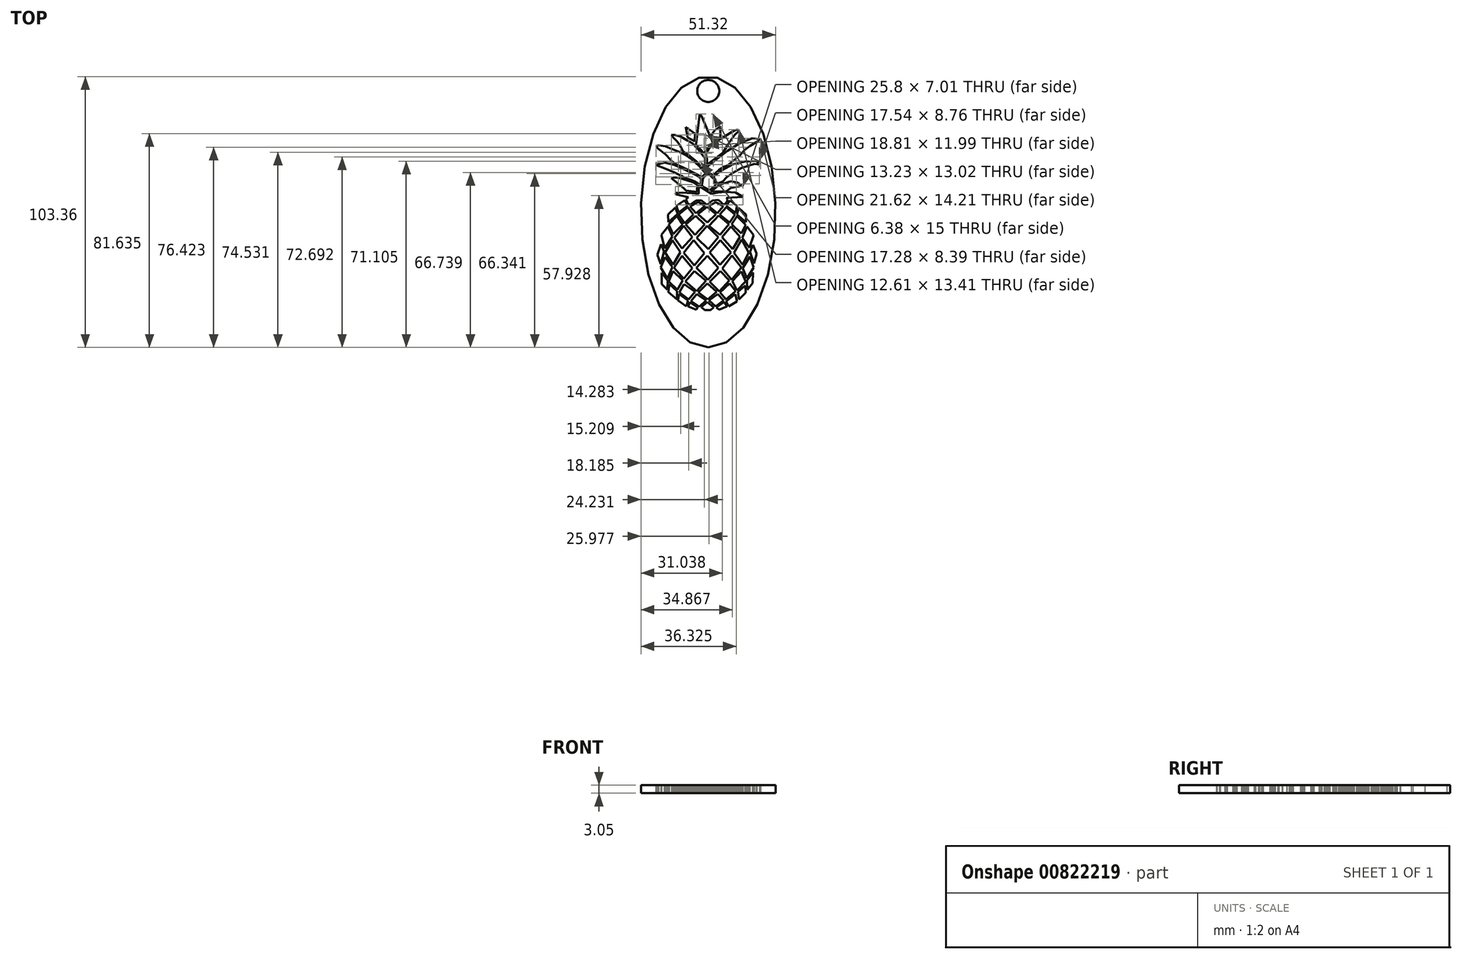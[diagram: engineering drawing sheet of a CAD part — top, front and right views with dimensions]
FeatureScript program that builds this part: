
annotation { "Feature Type Name" : "Feature", "Feature Type Description" : "" }
export const myFeature = defineFeature(function(context is Context, id is Id, definition is map)
    precondition{}
    {
        {
            var Q0;
            Q0=qCreatedBy(makeId("Top.planeOp"),FACE);
            var sketch = newSketch(context, id + "F0", { "sketchPlane" : qUnion([Q0])});
            skLineSegment(sketch, "E0", {"start": v(-25.66, -1.5) * mm, "end": v(-25.25, -6.5) * mm});
            skLineSegment(sketch, "E1", {"start": v(-25.25, -6.5) * mm, "end": v(-19.48, -1.16) * mm});
            skLineSegment(sketch, "E2", {"start": v(-19.48, -1.16) * mm, "end": v(-21, 2.9) * mm});
            skLineSegment(sketch, "E3", {"start": v(-21, 2.9) * mm, "end": v(-25.66, -1.5) * mm});
            skLineSegment(sketch, "E4", {"start": v(-20.22, 3.8) * mm, "end": v(-18.77, -0.42) * mm});
            skLineSegment(sketch, "E5", {"start": v(-18.77, -0.42) * mm, "end": v(-13.06, 4.15) * mm});
            skLineSegment(sketch, "E6", {"start": v(-13.06, 4.15) * mm, "end": v(-15.05, 7.52) * mm});
            skLineSegment(sketch, "E7", {"start": v(-15.05, 7.52) * mm, "end": v(-20.22, 3.8) * mm});
            skLineSegment(sketch, "E8", {"start": v(-18.89, -1.52) * mm, "end": v(-14.98, -7.06) * mm});
            skLineSegment(sketch, "E9", {"start": v(-14.98, -7.06) * mm, "end": v(-9.4, -1.52) * mm});
            skLineSegment(sketch, "E10", {"start": v(-9.4, -1.52) * mm, "end": v(-13.06, 3.14) * mm});
            skLineSegment(sketch, "E11", {"start": v(-13.06, 3.14) * mm, "end": v(-18.89, -1.52) * mm});
            skLineSegment(sketch, "E12", {"start": v(-25.2, -7.88) * mm, "end": v(-22.35, -14.06) * mm});
            skLineSegment(sketch, "E13", {"start": v(-22.35, -14.06) * mm, "end": v(-16.27, -7.88) * mm});
            skLineSegment(sketch, "E14", {"start": v(-16.27, -7.88) * mm, "end": v(-19.8, -2.51) * mm});
            skLineSegment(sketch, "E15", {"start": v(-19.8, -2.51) * mm, "end": v(-25.2, -7.88) * mm});
            skLineSegment(sketch, "E16", {"start": v(-25.66, -9.17) * mm, "end": v(-29.74, -14.43) * mm});
            skLineSegment(sketch, "E17", {"start": v(-29.74, -14.43) * mm, "end": v(-27.7, -23.26) * mm});
            skLineSegment(sketch, "E18", {"start": v(-27.7, -23.26) * mm, "end": v(-22.9, -15.5) * mm});
            skLineSegment(sketch, "E19", {"start": v(-22.9, -15.5) * mm, "end": v(-25.66, -9.17) * mm});
            skLineSegment(sketch, "E20", {"start": v(-21.48, -16.47) * mm, "end": v(-16.64, -23.26) * mm});
            skLineSegment(sketch, "E21", {"start": v(-16.64, -23.26) * mm, "end": v(-10.19, -16.03) * mm});
            skLineSegment(sketch, "E22", {"start": v(-10.19, -16.03) * mm, "end": v(-15.65, -8.87) * mm});
            skLineSegment(sketch, "E23", {"start": v(-15.65, -8.87) * mm, "end": v(-21.48, -16.47) * mm});
            skLineSegment(sketch, "E24", {"start": v(-30, -20.49) * mm, "end": v(-32.38, -27.19) * mm});
            skLineSegment(sketch, "E25", {"start": v(-32.38, -27.19) * mm, "end": v(-30.27, -33.09) * mm});
            skLineSegment(sketch, "E26", {"start": v(-30.27, -33.09) * mm, "end": v(-28.16, -24.99) * mm});
            skLineSegment(sketch, "E27", {"start": v(-28.16, -24.99) * mm, "end": v(-30, -20.49) * mm});
            skLineSegment(sketch, "E28", {"start": v(-27.43, -25.7) * mm, "end": v(-22.9, -17.8) * mm});
            skLineSegment(sketch, "E29", {"start": v(-22.9, -17.8) * mm, "end": v(-17.62, -25.44) * mm});
            skLineSegment(sketch, "E30", {"start": v(-17.62, -25.44) * mm, "end": v(-22.3, -33.55) * mm});
            skLineSegment(sketch, "E31", {"start": v(-22.3, -33.55) * mm, "end": v(-27.43, -25.7) * mm});
            skLineSegment(sketch, "E32", {"start": v(-29.58, -38.67) * mm, "end": v(-25.77, -43.74) * mm});
            skLineSegment(sketch, "E33", {"start": v(-25.77, -43.74) * mm, "end": v(-25.9, -49.5) * mm});
            skLineSegment(sketch, "E34", {"start": v(-25.9, -49.5) * mm, "end": v(-29.58, -45.83) * mm});
            skLineSegment(sketch, "E35", {"start": v(-29.58, -45.83) * mm, "end": v(-29.58, -38.67) * mm});
            skLineSegment(sketch, "E36", {"start": v(-25.89, -42.39) * mm, "end": v(-22.9, -35.09) * mm});
            skLineSegment(sketch, "E37", {"start": v(-22.9, -35.09) * mm, "end": v(-27.43, -28.61) * mm});
            skLineSegment(sketch, "E38", {"start": v(-27.43, -28.61) * mm, "end": v(-30.13, -35.18) * mm});
            skLineSegment(sketch, "E39", {"start": v(-30.13, -35.18) * mm, "end": v(-25.89, -42.39) * mm});
            skLineSegment(sketch, "E40", {"start": v(-25.06, -44.25) * mm, "end": v(-22.28, -37.5) * mm});
            skLineSegment(sketch, "E41", {"start": v(-22.28, -37.5) * mm, "end": v(-16.15, -43.49) * mm});
            skLineSegment(sketch, "E42", {"start": v(-16.15, -43.49) * mm, "end": v(-19.57, -49.5) * mm});
            skLineSegment(sketch, "E43", {"start": v(-19.57, -49.5) * mm, "end": v(-25.06, -44.25) * mm});
            skLineSegment(sketch, "E44", {"start": v(-24.8, -45.83) * mm, "end": v(-19.76, -50.26) * mm});
            skLineSegment(sketch, "E45", {"start": v(-19.76, -50.26) * mm, "end": v(-19.76, -55.47) * mm});
            skLineSegment(sketch, "E46", {"start": v(-19.76, -55.47) * mm, "end": v(-25.36, -50.95) * mm});
            skLineSegment(sketch, "E47", {"start": v(-25.36, -50.95) * mm, "end": v(-24.8, -45.83) * mm});
            skLineSegment(sketch, "E48", {"start": v(-19.16, -56.23) * mm, "end": v(-18.61, -52.19) * mm});
            skLineSegment(sketch, "E49", {"start": v(-18.61, -52.19) * mm, "end": v(-12.83, -56.23) * mm});
            skLineSegment(sketch, "E50", {"start": v(-12.83, -56.23) * mm, "end": v(-13.84, -60) * mm});
            skLineSegment(sketch, "E51", {"start": v(-13.84, -60) * mm, "end": v(-19.16, -56.23) * mm});
            skLineSegment(sketch, "E52", {"start": v(-11.6, -57.29) * mm, "end": v(-6.67, -60.45) * mm});
            skLineSegment(sketch, "E53", {"start": v(-6.67, -60.45) * mm, "end": v(-7.6, -62.06) * mm});
            skLineSegment(sketch, "E54", {"start": v(-7.6, -62.06) * mm, "end": v(-12.92, -60) * mm});
            skLineSegment(sketch, "E55", {"start": v(-12.92, -60) * mm, "end": v(-11.6, -57.29) * mm});
            skLineSegment(sketch, "E56", {"start": v(-2.29, -62.43) * mm, "end": v(1.52, -62.43) * mm});
            skLineSegment(sketch, "E57", {"start": v(1.52, -62.43) * mm, "end": v(3.43, -60.6) * mm});
            skLineSegment(sketch, "E58", {"start": v(3.43, -60.6) * mm, "end": v(-0.54, -57.17) * mm});
            skLineSegment(sketch, "E59", {"start": v(-0.54, -57.17) * mm, "end": v(-4.5, -60.45) * mm});
            skLineSegment(sketch, "E60", {"start": v(-4.5, -60.45) * mm, "end": v(-2.29, -62.43) * mm});
            skLineSegment(sketch, "E61", {"start": v(-5.7, -60.25) * mm, "end": v(-1.49, -56.3) * mm});
            skLineSegment(sketch, "E62", {"start": v(-1.49, -56.3) * mm, "end": v(-7.34, -52.19) * mm});
            skLineSegment(sketch, "E63", {"start": v(-7.34, -52.19) * mm, "end": v(-11.06, -56.55) * mm});
            skLineSegment(sketch, "E64", {"start": v(-11.06, -56.55) * mm, "end": v(-5.7, -60.25) * mm});
            skLineSegment(sketch, "E65", {"start": v(6.85, -62.06) * mm, "end": v(11.9, -60) * mm});
            skLineSegment(sketch, "E66", {"start": v(11.9, -60) * mm, "end": v(10.08, -57.17) * mm});
            skLineSegment(sketch, "E67", {"start": v(10.08, -57.17) * mm, "end": v(5.15, -60.68) * mm});
            skLineSegment(sketch, "E68", {"start": v(5.15, -60.68) * mm, "end": v(6.85, -62.06) * mm});
            skLineSegment(sketch, "E69", {"start": v(4.67, -60) * mm, "end": v(9.8, -56.22) * mm});
            skLineSegment(sketch, "E70", {"start": v(9.8, -56.22) * mm, "end": v(5.95, -52.19) * mm});
            skLineSegment(sketch, "E71", {"start": v(0.4, -56.22) * mm, "end": v(4.67, -60) * mm});
            skLineSegment(sketch, "E72", {"start": v(12.93, -60.09) * mm, "end": v(18.23, -56.83) * mm});
            skLineSegment(sketch, "E73", {"start": v(18.23, -56.83) * mm, "end": v(17.22, -52.19) * mm});
            skLineSegment(sketch, "E74", {"start": v(17.22, -52.19) * mm, "end": v(11.26, -56.78) * mm});
            skLineSegment(sketch, "E75", {"start": v(11.26, -56.78) * mm, "end": v(12.93, -60.09) * mm});
            skLineSegment(sketch, "E76", {"start": v(19.52, -55.6) * mm, "end": v(23.67, -51.43) * mm});
            skLineSegment(sketch, "E77", {"start": v(23.67, -51.43) * mm, "end": v(23.5, -46.61) * mm});
            skLineSegment(sketch, "E78", {"start": v(23.5, -46.61) * mm, "end": v(18.83, -50.6) * mm});
            skLineSegment(sketch, "E79", {"start": v(18.83, -50.6) * mm, "end": v(19.52, -55.6) * mm});
            skLineSegment(sketch, "E80", {"start": v(24.87, -49.48) * mm, "end": v(28.22, -45.16) * mm});
            skLineSegment(sketch, "E81", {"start": v(28.22, -45.16) * mm, "end": v(28.52, -38.53) * mm});
            skLineSegment(sketch, "E82", {"start": v(28.52, -38.53) * mm, "end": v(24.7, -43.42) * mm});
            skLineSegment(sketch, "E83", {"start": v(24.7, -43.42) * mm, "end": v(24.87, -49.48) * mm});
            skLineSegment(sketch, "E84", {"start": v(24.7, -42.23) * mm, "end": v(28.81, -35.16) * mm});
            skLineSegment(sketch, "E85", {"start": v(28.81, -35.16) * mm, "end": v(26.61, -28.25) * mm});
            skLineSegment(sketch, "E86", {"start": v(26.61, -28.25) * mm, "end": v(21.88, -35.61) * mm});
            skLineSegment(sketch, "E87", {"start": v(21.88, -35.61) * mm, "end": v(24.7, -42.23) * mm});
            skLineSegment(sketch, "E88", {"start": v(29.1, -32.7) * mm, "end": v(30.74, -26.55) * mm});
            skLineSegment(sketch, "E89", {"start": v(30.74, -26.55) * mm, "end": v(28.5, -20.78) * mm});
            skLineSegment(sketch, "E90", {"start": v(28.5, -20.78) * mm, "end": v(26.59, -25.37) * mm});
            skLineSegment(sketch, "E91", {"start": v(26.59, -25.37) * mm, "end": v(29.1, -32.7) * mm});
            skLineSegment(sketch, "E92", {"start": v(26.08, -22.69) * mm, "end": v(28.81, -14.65) * mm});
            skLineSegment(sketch, "E93", {"start": v(28.81, -14.65) * mm, "end": v(24.54, -9.28) * mm});
            skLineSegment(sketch, "E94", {"start": v(24.54, -9.28) * mm, "end": v(21.68, -16.37) * mm});
            skLineSegment(sketch, "E95", {"start": v(21.68, -16.37) * mm, "end": v(26.08, -22.69) * mm});
            skLineSegment(sketch, "E96", {"start": v(20.99, -13.69) * mm, "end": v(23.83, -8.2) * mm});
            skLineSegment(sketch, "E97", {"start": v(23.83, -8.2) * mm, "end": v(18.2, -2.6) * mm});
            skLineSegment(sketch, "E98", {"start": v(18.2, -2.6) * mm, "end": v(14.88, -7.74) * mm});
            skLineSegment(sketch, "E99", {"start": v(14.88, -7.74) * mm, "end": v(20.99, -13.69) * mm});
            skLineSegment(sketch, "E100", {"start": v(24.02, -6.48) * mm, "end": v(24.02, -1.54) * mm});
            skLineSegment(sketch, "E101", {"start": v(24.02, -1.54) * mm, "end": v(19.36, 2.68) * mm});
            skLineSegment(sketch, "E102", {"start": v(19.36, 2.68) * mm, "end": v(18.28, -1.59) * mm});
            skLineSegment(sketch, "E103", {"start": v(18.28, -1.59) * mm, "end": v(24.02, -6.48) * mm});
            skLineSegment(sketch, "E104", {"start": v(11.46, 3.92) * mm, "end": v(13.8, 7.2) * mm});
            skLineSegment(sketch, "E105", {"start": v(13.8, 7.2) * mm, "end": v(18.28, 3.92) * mm});
            skLineSegment(sketch, "E106", {"start": v(18.28, 3.92) * mm, "end": v(17.48, -0.47) * mm});
            skLineSegment(sketch, "E107", {"start": v(17.48, -0.47) * mm, "end": v(11.46, 3.92) * mm});
            skLineSegment(sketch, "E108", {"start": v(5.77, -0.72) * mm, "end": v(9.53, 3.67) * mm});
            skLineSegment(sketch, "E109", {"start": v(9.53, 3.67) * mm, "end": v(4.63, 6.14) * mm});
            skLineSegment(sketch, "E110", {"start": v(4.63, 6.14) * mm, "end": v(0.21, 3.76) * mm});
            skLineSegment(sketch, "E111", {"start": v(0.21, 3.76) * mm, "end": v(5.77, -0.72) * mm});
            skLineSegment(sketch, "E112", {"start": v(7.17, -1.68) * mm, "end": v(13.64, -6.64) * mm});
            skLineSegment(sketch, "E113", {"start": v(13.64, -6.64) * mm, "end": v(16.97, -1.68) * mm});
            skLineSegment(sketch, "E114", {"start": v(16.97, -1.68) * mm, "end": v(11.46, 3.12) * mm});
            skLineSegment(sketch, "E115", {"start": v(11.46, 3.12) * mm, "end": v(7.17, -1.68) * mm});
            skLineSegment(sketch, "E116", {"start": v(-11.65, 3.55) * mm, "end": v(-6.31, 6.44) * mm});
            skLineSegment(sketch, "E117", {"start": v(-6.31, 6.44) * mm, "end": v(-2.07, 3.81) * mm});
            skLineSegment(sketch, "E118", {"start": v(-2.07, 3.81) * mm, "end": v(-7.74, -0.72) * mm});
            skLineSegment(sketch, "E119", {"start": v(-7.74, -0.72) * mm, "end": v(-11.65, 3.55) * mm});
            skLineSegment(sketch, "E120", {"start": v(-14.43, -7.97) * mm, "end": v(-8.05, -2.34) * mm});
            skLineSegment(sketch, "E121", {"start": v(-8.05, -2.34) * mm, "end": v(-2.26, -7.97) * mm});
            skLineSegment(sketch, "E122", {"start": v(-2.26, -7.97) * mm, "end": v(-8.44, -14.46) * mm});
            skLineSegment(sketch, "E123", {"start": v(-8.44, -14.46) * mm, "end": v(-14.43, -7.97) * mm});
            skLineSegment(sketch, "E124", {"start": v(-6.53, -1.28) * mm, "end": v(-0.6, -6.64) * mm});
            skLineSegment(sketch, "E125", {"start": v(-0.6, -6.64) * mm, "end": v(4.87, -1.4) * mm});
            skLineSegment(sketch, "E126", {"start": v(4.87, -1.4) * mm, "end": v(-0.73, 3.37) * mm});
            skLineSegment(sketch, "E127", {"start": v(-0.73, 3.37) * mm, "end": v(-6.53, -1.28) * mm});
            skLineSegment(sketch, "E128", {"start": v(0.58, -8.69) * mm, "end": v(7.43, -14.46) * mm});
            skLineSegment(sketch, "E129", {"start": v(7.43, -14.46) * mm, "end": v(13.07, -7.72) * mm});
            skLineSegment(sketch, "E130", {"start": v(13.07, -7.72) * mm, "end": v(6.52, -2.19) * mm});
            skLineSegment(sketch, "E131", {"start": v(6.52, -2.19) * mm, "end": v(0.58, -8.69) * mm});
            skLineSegment(sketch, "E132", {"start": v(-7.39, -16.48) * mm, "end": v(-0.83, -8.87) * mm});
            skLineSegment(sketch, "E133", {"start": v(-0.83, -8.87) * mm, "end": v(6.37, -15.98) * mm});
            skLineSegment(sketch, "E134", {"start": v(6.37, -15.98) * mm, "end": v(0.02, -23.62) * mm});
            skLineSegment(sketch, "E135", {"start": v(0.02, -23.62) * mm, "end": v(-7.39, -16.48) * mm});
            skLineSegment(sketch, "E136", {"start": v(8.75, -15.98) * mm, "end": v(14.4, -9.28) * mm});
            skLineSegment(sketch, "E137", {"start": v(14.4, -9.28) * mm, "end": v(20.16, -15.77) * mm});
            skLineSegment(sketch, "E138", {"start": v(20.16, -15.77) * mm, "end": v(15.51, -23.62) * mm});
            skLineSegment(sketch, "E139", {"start": v(15.51, -23.62) * mm, "end": v(8.75, -15.98) * mm});
            skLineSegment(sketch, "E140", {"start": v(16.38, -25.9) * mm, "end": v(21.15, -17.57) * mm});
            skLineSegment(sketch, "E141", {"start": v(21.15, -17.57) * mm, "end": v(25.73, -25.67) * mm});
            skLineSegment(sketch, "E142", {"start": v(25.73, -25.67) * mm, "end": v(21.88, -33.55) * mm});
            skLineSegment(sketch, "E143", {"start": v(21.88, -33.55) * mm, "end": v(16.38, -25.9) * mm});
            skLineSegment(sketch, "E144", {"start": v(7.56, -33.55) * mm, "end": v(14.46, -25.67) * mm});
            skLineSegment(sketch, "E145", {"start": v(14.46, -25.67) * mm, "end": v(7.74, -17.8) * mm});
            skLineSegment(sketch, "E146", {"start": v(7.74, -17.8) * mm, "end": v(0.95, -25.67) * mm});
            skLineSegment(sketch, "E147", {"start": v(0.95, -25.67) * mm, "end": v(7.56, -33.55) * mm});
            skLineSegment(sketch, "E148", {"start": v(8.97, -35.82) * mm, "end": v(15.15, -27.62) * mm});
            skLineSegment(sketch, "E149", {"start": v(15.15, -27.62) * mm, "end": v(21.06, -35.24) * mm});
            skLineSegment(sketch, "E150", {"start": v(21.06, -35.24) * mm, "end": v(14.88, -43.05) * mm});
            skLineSegment(sketch, "E151", {"start": v(14.88, -43.05) * mm, "end": v(8.97, -35.82) * mm});
            skLineSegment(sketch, "E152", {"start": v(-8.93, -33.88) * mm, "end": v(-2.54, -26.12) * mm});
            skLineSegment(sketch, "E153", {"start": v(-2.54, -26.12) * mm, "end": v(-9.24, -17.8) * mm});
            skLineSegment(sketch, "E154", {"start": v(-9.24, -17.8) * mm, "end": v(-15.59, -25.84) * mm});
            skLineSegment(sketch, "E155", {"start": v(-15.59, -25.84) * mm, "end": v(-8.93, -33.88) * mm});
            skLineSegment(sketch, "E156", {"start": v(-21.8, -35.5) * mm, "end": v(-16.7, -27.93) * mm});
            skLineSegment(sketch, "E157", {"start": v(-16.7, -27.93) * mm, "end": v(-10.19, -35.65) * mm});
            skLineSegment(sketch, "E158", {"start": v(-10.19, -35.65) * mm, "end": v(-15.59, -42.39) * mm});
            skLineSegment(sketch, "E159", {"start": v(-15.59, -42.39) * mm, "end": v(-21.8, -35.5) * mm});
            skLineSegment(sketch, "E160", {"start": v(-7.65, -35.5) * mm, "end": v(-0.2, -43.05) * mm});
            skLineSegment(sketch, "E161", {"start": v(-0.2, -43.05) * mm, "end": v(6.37, -35.5) * mm});
            skLineSegment(sketch, "E162", {"start": v(6.37, -35.5) * mm, "end": v(-0.64, -27.93) * mm});
            skLineSegment(sketch, "E163", {"start": v(-14.49, -44.08) * mm, "end": v(-8.75, -37.5) * mm});
            skLineSegment(sketch, "E164", {"start": v(-8.75, -37.5) * mm, "end": v(-1.49, -43.71) * mm});
            skLineSegment(sketch, "E165", {"start": v(-1.49, -43.71) * mm, "end": v(-7.39, -50.2) * mm});
            skLineSegment(sketch, "E166", {"start": v(-7.39, -50.2) * mm, "end": v(-14.49, -44.08) * mm});
            skLineSegment(sketch, "E167", {"start": v(-18.32, -51.11) * mm, "end": v(-15.37, -45.83) * mm});
            skLineSegment(sketch, "E168", {"start": v(-15.37, -45.83) * mm, "end": v(-8.49, -50.65) * mm});
            skLineSegment(sketch, "E169", {"start": v(-8.49, -50.65) * mm, "end": v(-12.41, -55.6) * mm});
            skLineSegment(sketch, "E170", {"start": v(-12.41, -55.6) * mm, "end": v(-18.32, -51.11) * mm});
            skLineSegment(sketch, "E171", {"start": v(-6.27, -51.11) * mm, "end": v(-0.64, -45.48) * mm});
            skLineSegment(sketch, "E172", {"start": v(-0.64, -45.48) * mm, "end": v(5.45, -50.72) * mm});
            skLineSegment(sketch, "E173", {"start": v(5.45, -50.72) * mm, "end": v(-0.41, -55.6) * mm});
            skLineSegment(sketch, "E174", {"start": v(-0.41, -55.6) * mm, "end": v(-6.27, -51.11) * mm});
            skLineSegment(sketch, "E175", {"start": v(0.95, -44.29) * mm, "end": v(7.7, -37.5) * mm});
            skLineSegment(sketch, "E176", {"start": v(7.7, -37.5) * mm, "end": v(13.43, -43.5) * mm});
            skLineSegment(sketch, "E177", {"start": v(13.43, -43.5) * mm, "end": v(6.95, -50.54) * mm});
            skLineSegment(sketch, "E178", {"start": v(6.95, -50.54) * mm, "end": v(0.95, -44.29) * mm});
            skLineSegment(sketch, "E179", {"start": v(7.47, -51.11) * mm, "end": v(13.7, -45.48) * mm});
            skLineSegment(sketch, "E180", {"start": v(13.7, -45.48) * mm, "end": v(17.35, -50.2) * mm});
            skLineSegment(sketch, "E181", {"start": v(17.35, -50.2) * mm, "end": v(11.26, -55.6) * mm});
            skLineSegment(sketch, "E182", {"start": v(11.26, -55.6) * mm, "end": v(7.47, -51.11) * mm});
            skLineSegment(sketch, "E183", {"start": v(15.32, -43.85) * mm, "end": v(18.23, -49.93) * mm});
            skLineSegment(sketch, "E184", {"start": v(18.23, -49.93) * mm, "end": v(23.67, -44.08) * mm});
            skLineSegment(sketch, "E185", {"start": v(23.67, -44.08) * mm, "end": v(21.06, -37.85) * mm});
            skLineSegment(sketch, "E186", {"start": v(21.06, -37.85) * mm, "end": v(15.32, -43.85) * mm});
            skLineSegment(sketch, "E187", {"start": v(-0.83, 4.57) * mm, "end": v(2.5, 7.2) * mm});
            skLineSegment(sketch, "E188", {"start": v(2.5, 7.2) * mm, "end": v(6.37, 7.8) * mm});
            skLineSegment(sketch, "E189", {"start": v(6.37, 7.8) * mm, "end": v(9.9, 4.57) * mm});
            skLineSegment(sketch, "E190", {"start": v(9.9, 4.57) * mm, "end": v(11.62, 6.2) * mm});
            skLineSegment(sketch, "E191", {"start": v(11.62, 6.2) * mm, "end": v(12.33, 7.83) * mm});
            skLineSegment(sketch, "E192", {"start": v(12.33, 7.83) * mm, "end": v(11.46, 9.03) * mm});
            skLineSegment(sketch, "E193", {"start": v(11.46, 9.03) * mm, "end": v(22.03, 9.55) * mm});
            skLineSegment(sketch, "E194", {"start": v(22.03, 9.55) * mm, "end": v(17.4, 12.38) * mm});
            skLineSegment(sketch, "E195", {"start": v(17.4, 12.38) * mm, "end": v(11, 12.77) * mm});
            skLineSegment(sketch, "E196", {"start": v(11, 12.77) * mm, "end": v(6.02, 12.42) * mm});
            skLineSegment(sketch, "E197", {"start": v(6.02, 12.42) * mm, "end": v(2.27, 11.63) * mm});
            skLineSegment(sketch, "E198", {"start": v(2.27, 11.63) * mm, "end": v(-5.18, 16.26) * mm});
            skLineSegment(sketch, "E199", {"start": v(-5.18, 16.26) * mm, "end": v(-6.15, 15.07) * mm});
            skLineSegment(sketch, "E200", {"start": v(-6.15, 15.07) * mm, "end": v(-6.15, 11.58) * mm});
            skLineSegment(sketch, "E201", {"start": v(-6.15, 11.58) * mm, "end": v(-10.37, 11.86) * mm});
            skLineSegment(sketch, "E202", {"start": v(-10.37, 11.86) * mm, "end": v(-16.64, 12.47) * mm});
            skLineSegment(sketch, "E203", {"start": v(-16.64, 12.47) * mm, "end": v(-20.48, 12.16) * mm});
            skLineSegment(sketch, "E204", {"start": v(-20.48, 12.16) * mm, "end": v(-20.97, 11.4) * mm});
            skLineSegment(sketch, "E205", {"start": v(-20.97, 11.4) * mm, "end": v(-12.59, 9.51) * mm});
            skLineSegment(sketch, "E206", {"start": v(-12.59, 9.51) * mm, "end": v(-14.15, 8.1) * mm});
            skLineSegment(sketch, "E207", {"start": v(-14.15, 8.1) * mm, "end": v(-13.25, 5.8) * mm});
            skLineSegment(sketch, "E208", {"start": v(-13.25, 5.8) * mm, "end": v(-11.65, 4.57) * mm});
            skLineSegment(sketch, "E209", {"start": v(-11.65, 4.57) * mm, "end": v(-7.78, 7.2) * mm});
            skLineSegment(sketch, "E210", {"start": v(-7.78, 7.2) * mm, "end": v(-4.65, 7.52) * mm});
            skLineSegment(sketch, "E211", {"start": v(-4.65, 7.52) * mm, "end": v(-0.83, 4.57) * mm});
            skLineSegment(sketch, "E212", {"start": v(1.74, 13.08) * mm, "end": v(11.46, 13.3) * mm});
            skLineSegment(sketch, "E213", {"start": v(11.46, 13.3) * mm, "end": v(14.46, 15.33) * mm});
            skLineSegment(sketch, "E214", {"start": v(14.46, 15.33) * mm, "end": v(19.36, 16.26) * mm});
            skLineSegment(sketch, "E215", {"start": v(19.36, 16.26) * mm, "end": v(21.15, 16.87) * mm});
            skLineSegment(sketch, "E216", {"start": v(21.15, 16.87) * mm, "end": v(18.28, 18.73) * mm});
            skLineSegment(sketch, "E217", {"start": v(18.28, 18.73) * mm, "end": v(14.46, 19.65) * mm});
            skLineSegment(sketch, "E218", {"start": v(14.46, 19.65) * mm, "end": v(9.63, 18.18) * mm});
            skLineSegment(sketch, "E219", {"start": v(9.63, 18.18) * mm, "end": v(6.1, 16.66) * mm});
            skLineSegment(sketch, "E220", {"start": v(6.1, 16.66) * mm, "end": v(1.74, 13.08) * mm});
            skLineSegment(sketch, "E221", {"start": v(-23.48, 21.37) * mm, "end": v(-19.48, 18.33) * mm});
            skLineSegment(sketch, "E222", {"start": v(-19.48, 18.33) * mm, "end": v(-15.37, 14.98) * mm});
            skLineSegment(sketch, "E223", {"start": v(-15.37, 14.98) * mm, "end": v(-14.21, 13.6) * mm});
            skLineSegment(sketch, "E224", {"start": v(-14.21, 13.6) * mm, "end": v(-7.17, 12.86) * mm});
            skLineSegment(sketch, "E225", {"start": v(-7.17, 12.86) * mm, "end": v(-7.17, 14.85) * mm});
            skLineSegment(sketch, "E226", {"start": v(-7.17, 14.85) * mm, "end": v(-6.53, 16.79) * mm});
            skLineSegment(sketch, "E227", {"start": v(-6.53, 16.79) * mm, "end": v(-9.74, 19) * mm});
            skLineSegment(sketch, "E228", {"start": v(-9.74, 19) * mm, "end": v(-19.12, 22) * mm});
            skLineSegment(sketch, "E229", {"start": v(-19.12, 22) * mm, "end": v(-21.98, 22) * mm});
            skLineSegment(sketch, "E230", {"start": v(-21.98, 22) * mm, "end": v(-23.48, 21.37) * mm});
            skLineSegment(sketch, "E231", {"start": v(-4.08, 16.61) * mm, "end": v(0.95, 13.79) * mm});
            skLineSegment(sketch, "E232", {"start": v(0.95, 13.79) * mm, "end": v(4.65, 16.96) * mm});
            skLineSegment(sketch, "E233", {"start": v(4.65, 16.96) * mm, "end": v(3.6, 20.78) * mm});
            skLineSegment(sketch, "E234", {"start": v(3.6, 20.78) * mm, "end": v(-0.1, 24.61) * mm});
            skLineSegment(sketch, "E235", {"start": v(-0.1, 24.61) * mm, "end": v(-3.27, 21.5) * mm});
            skLineSegment(sketch, "E236", {"start": v(-3.27, 21.5) * mm, "end": v(-4.08, 16.61) * mm});
            skLineSegment(sketch, "E237", {"start": v(-33.36, 29.93) * mm, "end": v(-26.88, 27.46) * mm});
            skLineSegment(sketch, "E238", {"start": v(-26.88, 27.46) * mm, "end": v(-21.85, 25.2) * mm});
            skLineSegment(sketch, "E239", {"start": v(-21.85, 25.2) * mm, "end": v(-17, 22.92) * mm});
            skLineSegment(sketch, "E240", {"start": v(-17, 22.92) * mm, "end": v(-15, 21.64) * mm});
            skLineSegment(sketch, "E241", {"start": v(-11.65, 20.71) * mm, "end": v(-8.8, 19.65) * mm});
            skLineSegment(sketch, "E242", {"start": v(-8.8, 19.65) * mm, "end": v(-6.86, 18.42) * mm});
            skLineSegment(sketch, "E243", {"start": v(-6.86, 18.42) * mm, "end": v(-6.33, 17.44) * mm});
            skLineSegment(sketch, "E244", {"start": v(-6.33, 17.44) * mm, "end": v(-4.96, 17.44) * mm});
            skLineSegment(sketch, "E245", {"start": v(-4.96, 17.44) * mm, "end": v(-4.65, 20.05) * mm});
            skLineSegment(sketch, "E246", {"start": v(-4.65, 20.05) * mm, "end": v(-4.56, 21.36) * mm});
            skLineSegment(sketch, "E247", {"start": v(-4.56, 21.36) * mm, "end": v(-7.65, 23.31) * mm});
            skLineSegment(sketch, "E248", {"start": v(-7.65, 23.31) * mm, "end": v(-14.15, 26.58) * mm});
            skLineSegment(sketch, "E249", {"start": v(-14.15, 26.58) * mm, "end": v(-21.5, 29.93) * mm});
            skLineSegment(sketch, "E250", {"start": v(-21.5, 29.93) * mm, "end": v(-27.76, 31.43) * mm});
            skLineSegment(sketch, "E251", {"start": v(-27.76, 31.43) * mm, "end": v(-33.36, 29.93) * mm});
            skLineSegment(sketch, "E252", {"start": v(5.14, 17.8) * mm, "end": v(9.06, 19.26) * mm});
            skLineSegment(sketch, "E253", {"start": v(9.06, 19.26) * mm, "end": v(11.7, 22.02) * mm});
            skLineSegment(sketch, "E254", {"start": v(11.7, 22.02) * mm, "end": v(16.03, 25.08) * mm});
            skLineSegment(sketch, "E255", {"start": v(16.03, 25.08) * mm, "end": v(21.15, 27.99) * mm});
            skLineSegment(sketch, "E256", {"start": v(21.15, 27.99) * mm, "end": v(29.3, 30.68) * mm});
            skLineSegment(sketch, "E257", {"start": v(29.3, 30.68) * mm, "end": v(32.39, 30.24) * mm});
            skLineSegment(sketch, "E258", {"start": v(32.39, 30.24) * mm, "end": v(30.93, 32.4) * mm});
            skLineSegment(sketch, "E259", {"start": v(30.93, 32.4) * mm, "end": v(23.13, 32.04) * mm});
            skLineSegment(sketch, "E260", {"start": v(23.13, 32.04) * mm, "end": v(15.2, 30.1) * mm});
            skLineSegment(sketch, "E261", {"start": v(15.2, 30.1) * mm, "end": v(8.67, 26.46) * mm});
            skLineSegment(sketch, "E262", {"start": v(8.67, 26.46) * mm, "end": v(3.16, 22.61) * mm});
            skLineSegment(sketch, "E263", {"start": v(3.16, 22.61) * mm, "end": v(4.21, 21.06) * mm});
            skLineSegment(sketch, "E264", {"start": v(4.21, 21.06) * mm, "end": v(5.14, 17.8) * mm});
            skLineSegment(sketch, "E265", {"start": v(-4.08, 22.39) * mm, "end": v(-1.74, 24.43) * mm});
            skLineSegment(sketch, "E266", {"start": v(-1.74, 24.43) * mm, "end": v(-5.76, 29.08) * mm});
            skLineSegment(sketch, "E267", {"start": v(-5.76, 29.08) * mm, "end": v(-10.38, 33.28) * mm});
            skLineSegment(sketch, "E268", {"start": v(-10.38, 33.28) * mm, "end": v(-14.53, 36.23) * mm});
            skLineSegment(sketch, "E269", {"start": v(-14.53, 36.23) * mm, "end": v(-18.28, 38.22) * mm});
            skLineSegment(sketch, "E270", {"start": v(-18.28, 38.22) * mm, "end": v(-23.22, 40.07) * mm});
            skLineSegment(sketch, "E271", {"start": v(-23.22, 40.07) * mm, "end": v(-27.32, 41.75) * mm});
            skLineSegment(sketch, "E272", {"start": v(-27.32, 41.75) * mm, "end": v(-31.55, 42.36) * mm});
            skLineSegment(sketch, "E273", {"start": v(-31.55, 42.36) * mm, "end": v(-33.1, 42.1) * mm});
            skLineSegment(sketch, "E274", {"start": v(-33.1, 42.1) * mm, "end": v(-31.82, 40.3) * mm});
            skLineSegment(sketch, "E275", {"start": v(-31.82, 40.3) * mm, "end": v(-27.54, 37.03) * mm});
            skLineSegment(sketch, "E276", {"start": v(-27.54, 37.03) * mm, "end": v(-23.48, 32.8) * mm});
            skLineSegment(sketch, "E277", {"start": v(-23.48, 32.8) * mm, "end": v(-20.84, 30.54) * mm});
            skLineSegment(sketch, "E278", {"start": v(-20.84, 30.54) * mm, "end": v(-12.99, 27.06) * mm});
            skLineSegment(sketch, "E279", {"start": v(-12.99, 27.06) * mm, "end": v(-4.08, 22.39) * mm});
            skLineSegment(sketch, "E280", {"start": v(-3.33, 27.24) * mm, "end": v(-1.43, 29.13) * mm});
            skLineSegment(sketch, "E281", {"start": v(-1.43, 29.13) * mm, "end": v(-2.2, 34.34) * mm});
            skLineSegment(sketch, "E282", {"start": v(-2.2, 34.34) * mm, "end": v(-6.55, 39.96) * mm});
            skLineSegment(sketch, "E283", {"start": v(-6.55, 39.96) * mm, "end": v(-10.03, 43.69) * mm});
            skLineSegment(sketch, "E284", {"start": v(-10.03, 43.69) * mm, "end": v(-13.43, 45.67) * mm});
            skLineSegment(sketch, "E285", {"start": v(-13.43, 45.67) * mm, "end": v(-17.62, 47.83) * mm});
            skLineSegment(sketch, "E286", {"start": v(-17.62, 47.83) * mm, "end": v(-21.05, 48.93) * mm});
            skLineSegment(sketch, "E287", {"start": v(-21.05, 48.93) * mm, "end": v(-23.48, 48.93) * mm});
            skLineSegment(sketch, "E288", {"start": v(-23.48, 48.93) * mm, "end": v(-22.11, 47.21) * mm});
            skLineSegment(sketch, "E289", {"start": v(-22.11, 47.21) * mm, "end": v(-19.95, 45.23) * mm});
            skLineSegment(sketch, "E290", {"start": v(-19.95, 45.23) * mm, "end": v(-18.01, 42.38) * mm});
            skLineSegment(sketch, "E291", {"start": v(-18.01, 42.38) * mm, "end": v(-15.94, 38.48) * mm});
            skLineSegment(sketch, "E292", {"start": v(-15.94, 38.48) * mm, "end": v(-11.75, 35.75) * mm});
            skLineSegment(sketch, "E293", {"start": v(-11.75, 35.75) * mm, "end": v(-7.43, 32.09) * mm});
            skLineSegment(sketch, "E294", {"start": v(-7.43, 32.09) * mm, "end": v(-3.33, 27.24) * mm});
            skLineSegment(sketch, "E295", {"start": v(-2.67, 26.66) * mm, "end": v(-1.43, 25.1) * mm});
            skLineSegment(sketch, "E296", {"start": v(-1.43, 25.1) * mm, "end": v(0.49, 25.1) * mm});
            skLineSegment(sketch, "E297", {"start": v(0.49, 25.1) * mm, "end": v(1.74, 24.2) * mm});
            skLineSegment(sketch, "E298", {"start": v(1.74, 24.2) * mm, "end": v(2.4, 23.18) * mm});
            skLineSegment(sketch, "E299", {"start": v(2.4, 23.18) * mm, "end": v(4.65, 24.92) * mm});
            skLineSegment(sketch, "E300", {"start": v(4.65, 24.92) * mm, "end": v(6.86, 26.66) * mm});
            skLineSegment(sketch, "E301", {"start": v(6.86, 26.66) * mm, "end": v(10.2, 28.78) * mm});
            skLineSegment(sketch, "E302", {"start": v(10.2, 28.78) * mm, "end": v(12.2, 29.49) * mm});
            skLineSegment(sketch, "E303", {"start": v(12.2, 29.49) * mm, "end": v(19.9, 35.84) * mm});
            skLineSegment(sketch, "E304", {"start": v(19.9, 35.84) * mm, "end": v(23.08, 39.4) * mm});
            skLineSegment(sketch, "E305", {"start": v(23.08, 39.4) * mm, "end": v(26.57, 42.1) * mm});
            skLineSegment(sketch, "E306", {"start": v(26.57, 42.1) * mm, "end": v(30.36, 44.4) * mm});
            skLineSegment(sketch, "E307", {"start": v(30.36, 44.4) * mm, "end": v(33.36, 46.38) * mm});
            skLineSegment(sketch, "E308", {"start": v(33.36, 46.38) * mm, "end": v(27.94, 46.86) * mm});
            skLineSegment(sketch, "E309", {"start": v(27.94, 46.86) * mm, "end": v(19.87, 43.6) * mm});
            skLineSegment(sketch, "E310", {"start": v(19.87, 43.6) * mm, "end": v(12.06, 38.75) * mm});
            skLineSegment(sketch, "E311", {"start": v(12.06, 38.75) * mm, "end": v(4.52, 32.93) * mm});
            skLineSegment(sketch, "E312", {"start": v(4.52, 32.93) * mm, "end": v(0.17, 29.6) * mm});
            skLineSegment(sketch, "E313", {"start": v(0.17, 29.6) * mm, "end": v(-2.67, 26.66) * mm});
            skLineSegment(sketch, "E314", {"start": v(-0.77, 30.06) * mm, "end": v(-0.77, 33.76) * mm});
            skLineSegment(sketch, "E315", {"start": v(-0.77, 33.76) * mm, "end": v(-1.54, 37.02) * mm});
            skLineSegment(sketch, "E316", {"start": v(-1.54, 37.02) * mm, "end": v(0.29, 40.16) * mm});
            skLineSegment(sketch, "E317", {"start": v(0.29, 40.16) * mm, "end": v(2.84, 42.85) * mm});
            skLineSegment(sketch, "E318", {"start": v(2.84, 42.85) * mm, "end": v(5.36, 44.79) * mm});
            skLineSegment(sketch, "E319", {"start": v(5.36, 44.79) * mm, "end": v(8.58, 46.9) * mm});
            skLineSegment(sketch, "E320", {"start": v(8.58, 46.9) * mm, "end": v(11.97, 48.89) * mm});
            skLineSegment(sketch, "E321", {"start": v(11.97, 48.89) * mm, "end": v(14.7, 50.65) * mm});
            skLineSegment(sketch, "E322", {"start": v(14.7, 50.65) * mm, "end": v(16.73, 51.89) * mm});
            skLineSegment(sketch, "E323", {"start": v(16.73, 51.89) * mm, "end": v(18.98, 52.42) * mm});
            skLineSegment(sketch, "E324", {"start": v(18.98, 52.42) * mm, "end": v(19.47, 51.45) * mm});
            skLineSegment(sketch, "E325", {"start": v(19.47, 51.45) * mm, "end": v(16.91, 49.11) * mm});
            skLineSegment(sketch, "E326", {"start": v(16.91, 49.11) * mm, "end": v(14.97, 46.46) * mm});
            skLineSegment(sketch, "E327", {"start": v(14.97, 46.46) * mm, "end": v(12.41, 42.67) * mm});
            skLineSegment(sketch, "E328", {"start": v(12.41, 42.67) * mm, "end": v(9.33, 37.82) * mm});
            skLineSegment(sketch, "E329", {"start": v(9.33, 37.82) * mm, "end": v(-0.77, 30.06) * mm});
            skLineSegment(sketch, "E330", {"start": v(-2.67, 37.42) * mm, "end": v(-0.33, 40.73) * mm});
            skLineSegment(sketch, "E331", {"start": v(-0.33, 40.73) * mm, "end": v(2.93, 44) * mm});
            skLineSegment(sketch, "E332", {"start": v(2.93, 44) * mm, "end": v(-4.39, 61.28) * mm});
            skLineSegment(sketch, "E333", {"start": v(-4.39, 61.28) * mm, "end": v(-5.53, 62.43) * mm});
            skLineSegment(sketch, "E334", {"start": v(-5.53, 62.43) * mm, "end": v(-7.7, 42.9) * mm});
            skLineSegment(sketch, "E335", {"start": v(-7.7, 42.9) * mm, "end": v(-2.67, 37.42) * mm});
            skLineSegment(sketch, "E336", {"start": v(-8.7, 44.88) * mm, "end": v(-8.31, 49.76) * mm});
            skLineSegment(sketch, "E337", {"start": v(-8.31, 49.76) * mm, "end": v(-14.35, 54.1) * mm});
            skLineSegment(sketch, "E338", {"start": v(-14.35, 54.1) * mm, "end": v(-13.43, 49.64) * mm});
            skLineSegment(sketch, "E339", {"start": v(-13.43, 49.64) * mm, "end": v(-13.28, 47.43) * mm});
            skLineSegment(sketch, "E340", {"start": v(-13.28, 47.43) * mm, "end": v(-8.7, 44.88) * mm});
            skLineSegment(sketch, "E341", {"start": v(3.73, 45.15) * mm, "end": v(7.7, 47.96) * mm});
            skLineSegment(sketch, "E342", {"start": v(7.7, 47.96) * mm, "end": v(7.7, 50.65) * mm});
            skLineSegment(sketch, "E343", {"start": v(7.7, 50.65) * mm, "end": v(7.7, 54.58) * mm});
            skLineSegment(sketch, "E344", {"start": v(7.7, 54.58) * mm, "end": v(4.03, 51.98) * mm});
            skLineSegment(sketch, "E345", {"start": v(4.03, 51.98) * mm, "end": v(1.93, 49.02) * mm});
            skLineSegment(sketch, "E346", {"start": v(1.93, 49.02) * mm, "end": v(3.73, 45.15) * mm});
            skLineSegment(sketch, "E347", {"start": v(-7.65, -35.5) * mm, "end": v(-0.64, -27.93) * mm});
            skLineSegment(sketch, "E348.bottom", {"start": v(-35.04, -65.92) * mm, "end": v(35.04, -65.92) * mm, "construction": true});
            skLineSegment(sketch, "E348.top", {"start": v(-35.04, 65.18) * mm, "end": v(35.04, 65.18) * mm, "construction": true});
            skLineSegment(sketch, "E348.left", {"start": v(-35.04, -65.92) * mm, "end": v(-35.04, 65.18) * mm, "construction": true});
            skLineSegment(sketch, "E348.right", {"start": v(35.04, -65.92) * mm, "end": v(35.04, 65.18) * mm, "construction": true});
            skEllipse(sketch, "E349", {"center": v(0, 0) * mm, "majorRadius": 86.13 * mm, "minorRadius": 42.76 * mm, "majorAxis": v(0, -1)});
            skCircle(sketch, "E350", {"center": v(0, 76.96) * mm, "radius": 6.99 * mm});
            skLineSegment(sketch, "E351", {"start": v(42.76, -0.37) * mm, "end": v(-42.76, -0.37) * mm, "construction": true});
            skPoint(sketch, "E351.startSnap0", {"position": v(35.04, -0.37) * mm});
            skLineSegment(sketch, "E352", {"start": v(0.4, -56.22) * mm, "end": v(5.95, -52.19) * mm});
            skLineSegment(sketch, "E353", {"start": v(-15, 21.64) * mm, "end": v(-11.65, 20.71) * mm});
            skLineSegment(sketch, "E354", {"start": v(-42.76, 0) * mm, "end": v(42.76, 0) * mm, "construction": true});
            skLineSegment(sketch, "E355", {"start": v(0, 86.13) * mm, "end": v(0, 83.94) * mm});
            skSolve(sketch);
        }
        {
            var Q0;
            Q0=makeQuery(id+"F0.imprint","IMPRINT",FACE,{"disambiguationData":[TD([[makeQuery(id+"F0.imprint","IMPRINT",EDGE,{"derivedFrom":sQuery(id+"F0.wireOp",EDGE,"E0")}),-1.0]])]});
            extrude(context, id + "F1", {"entities" : qUnion([Q0]), "depth" : 5.08 * mm, "offsetDistance" : 25.4 * mm});
        }
        {
            var Q0;
            Q0=makeQuery(id+"F1.opExtrude","SWEPT_BODY",BODY,{"disambiguationData":[OSD([sQuery(id+"F0.wireOp",EDGE,"E0"),sQuery(id+"F0.wireOp",EDGE,"E1"),sQuery(id+"F0.wireOp",EDGE,"E2"),sQuery(id+"F0.wireOp",EDGE,"E3"),sQuery(id+"F0.wireOp",EDGE,"E4"),sQuery(id+"F0.wireOp",EDGE,"E5"),sQuery(id+"F0.wireOp",EDGE,"E6"),sQuery(id+"F0.wireOp",EDGE,"E7"),sQuery(id+"F0.wireOp",EDGE,"E8"),sQuery(id+"F0.wireOp",EDGE,"E9"),sQuery(id+"F0.wireOp",EDGE,"E10"),sQuery(id+"F0.wireOp",EDGE,"E11"),sQuery(id+"F0.wireOp",EDGE,"E12"),sQuery(id+"F0.wireOp",EDGE,"E13"),sQuery(id+"F0.wireOp",EDGE,"E14"),sQuery(id+"F0.wireOp",EDGE,"E15"),sQuery(id+"F0.wireOp",EDGE,"E16"),sQuery(id+"F0.wireOp",EDGE,"E17"),sQuery(id+"F0.wireOp",EDGE,"E18"),sQuery(id+"F0.wireOp",EDGE,"E19"),sQuery(id+"F0.wireOp",EDGE,"E20"),sQuery(id+"F0.wireOp",EDGE,"E21"),sQuery(id+"F0.wireOp",EDGE,"E22"),sQuery(id+"F0.wireOp",EDGE,"E23"),sQuery(id+"F0.wireOp",EDGE,"E24"),sQuery(id+"F0.wireOp",EDGE,"E25"),sQuery(id+"F0.wireOp",EDGE,"E26"),sQuery(id+"F0.wireOp",EDGE,"E27"),sQuery(id+"F0.wireOp",EDGE,"E28"),sQuery(id+"F0.wireOp",EDGE,"E29"),sQuery(id+"F0.wireOp",EDGE,"E30"),sQuery(id+"F0.wireOp",EDGE,"E31"),sQuery(id+"F0.wireOp",EDGE,"E32"),sQuery(id+"F0.wireOp",EDGE,"E33"),sQuery(id+"F0.wireOp",EDGE,"E34"),sQuery(id+"F0.wireOp",EDGE,"E35"),sQuery(id+"F0.wireOp",EDGE,"E36"),sQuery(id+"F0.wireOp",EDGE,"E37"),sQuery(id+"F0.wireOp",EDGE,"E38"),sQuery(id+"F0.wireOp",EDGE,"E39"),sQuery(id+"F0.wireOp",EDGE,"E40"),sQuery(id+"F0.wireOp",EDGE,"E41"),sQuery(id+"F0.wireOp",EDGE,"E42"),sQuery(id+"F0.wireOp",EDGE,"E43"),sQuery(id+"F0.wireOp",EDGE,"E44"),sQuery(id+"F0.wireOp",EDGE,"E45"),sQuery(id+"F0.wireOp",EDGE,"E46"),sQuery(id+"F0.wireOp",EDGE,"E47"),sQuery(id+"F0.wireOp",EDGE,"E48"),sQuery(id+"F0.wireOp",EDGE,"E49"),sQuery(id+"F0.wireOp",EDGE,"E50"),sQuery(id+"F0.wireOp",EDGE,"E51"),sQuery(id+"F0.wireOp",EDGE,"E52"),sQuery(id+"F0.wireOp",EDGE,"E53"),sQuery(id+"F0.wireOp",EDGE,"E54"),sQuery(id+"F0.wireOp",EDGE,"E55"),sQuery(id+"F0.wireOp",EDGE,"E56"),sQuery(id+"F0.wireOp",EDGE,"E57"),sQuery(id+"F0.wireOp",EDGE,"E58"),sQuery(id+"F0.wireOp",EDGE,"E59"),sQuery(id+"F0.wireOp",EDGE,"E60"),sQuery(id+"F0.wireOp",EDGE,"E61"),sQuery(id+"F0.wireOp",EDGE,"E62"),sQuery(id+"F0.wireOp",EDGE,"E63"),sQuery(id+"F0.wireOp",EDGE,"E64"),sQuery(id+"F0.wireOp",EDGE,"E65"),sQuery(id+"F0.wireOp",EDGE,"E66"),sQuery(id+"F0.wireOp",EDGE,"E67"),sQuery(id+"F0.wireOp",EDGE,"E68"),sQuery(id+"F0.wireOp",EDGE,"E72"),sQuery(id+"F0.wireOp",EDGE,"E73"),sQuery(id+"F0.wireOp",EDGE,"E74"),sQuery(id+"F0.wireOp",EDGE,"E75"),sQuery(id+"F0.wireOp",EDGE,"E76"),sQuery(id+"F0.wireOp",EDGE,"E77"),sQuery(id+"F0.wireOp",EDGE,"E78"),sQuery(id+"F0.wireOp",EDGE,"E79"),sQuery(id+"F0.wireOp",EDGE,"E80"),sQuery(id+"F0.wireOp",EDGE,"E81"),sQuery(id+"F0.wireOp",EDGE,"E82"),sQuery(id+"F0.wireOp",EDGE,"E83"),sQuery(id+"F0.wireOp",EDGE,"E84"),sQuery(id+"F0.wireOp",EDGE,"E85"),sQuery(id+"F0.wireOp",EDGE,"E86"),sQuery(id+"F0.wireOp",EDGE,"E87"),sQuery(id+"F0.wireOp",EDGE,"E88"),sQuery(id+"F0.wireOp",EDGE,"E89"),sQuery(id+"F0.wireOp",EDGE,"E90"),sQuery(id+"F0.wireOp",EDGE,"E91"),sQuery(id+"F0.wireOp",EDGE,"E92"),sQuery(id+"F0.wireOp",EDGE,"E93"),sQuery(id+"F0.wireOp",EDGE,"E94"),sQuery(id+"F0.wireOp",EDGE,"E95"),sQuery(id+"F0.wireOp",EDGE,"E96"),sQuery(id+"F0.wireOp",EDGE,"E97"),sQuery(id+"F0.wireOp",EDGE,"E98"),sQuery(id+"F0.wireOp",EDGE,"E99"),sQuery(id+"F0.wireOp",EDGE,"E100"),sQuery(id+"F0.wireOp",EDGE,"E101"),sQuery(id+"F0.wireOp",EDGE,"E102"),sQuery(id+"F0.wireOp",EDGE,"E103"),sQuery(id+"F0.wireOp",EDGE,"E104"),sQuery(id+"F0.wireOp",EDGE,"E105"),sQuery(id+"F0.wireOp",EDGE,"E106"),sQuery(id+"F0.wireOp",EDGE,"E107"),sQuery(id+"F0.wireOp",EDGE,"E108"),sQuery(id+"F0.wireOp",EDGE,"E109"),sQuery(id+"F0.wireOp",EDGE,"E110"),sQuery(id+"F0.wireOp",EDGE,"E111"),sQuery(id+"F0.wireOp",EDGE,"E112"),sQuery(id+"F0.wireOp",EDGE,"E113"),sQuery(id+"F0.wireOp",EDGE,"E114"),sQuery(id+"F0.wireOp",EDGE,"E115"),sQuery(id+"F0.wireOp",EDGE,"E116"),sQuery(id+"F0.wireOp",EDGE,"E117"),sQuery(id+"F0.wireOp",EDGE,"E118"),sQuery(id+"F0.wireOp",EDGE,"E119"),sQuery(id+"F0.wireOp",EDGE,"E120"),sQuery(id+"F0.wireOp",EDGE,"E121"),sQuery(id+"F0.wireOp",EDGE,"E122"),sQuery(id+"F0.wireOp",EDGE,"E123"),sQuery(id+"F0.wireOp",EDGE,"E124"),sQuery(id+"F0.wireOp",EDGE,"E125"),sQuery(id+"F0.wireOp",EDGE,"E126"),sQuery(id+"F0.wireOp",EDGE,"E127"),sQuery(id+"F0.wireOp",EDGE,"E128"),sQuery(id+"F0.wireOp",EDGE,"E129"),sQuery(id+"F0.wireOp",EDGE,"E130"),sQuery(id+"F0.wireOp",EDGE,"E131"),sQuery(id+"F0.wireOp",EDGE,"E132"),sQuery(id+"F0.wireOp",EDGE,"E133"),sQuery(id+"F0.wireOp",EDGE,"E134"),sQuery(id+"F0.wireOp",EDGE,"E135"),sQuery(id+"F0.wireOp",EDGE,"E136"),sQuery(id+"F0.wireOp",EDGE,"E137"),sQuery(id+"F0.wireOp",EDGE,"E138"),sQuery(id+"F0.wireOp",EDGE,"E139"),sQuery(id+"F0.wireOp",EDGE,"E140"),sQuery(id+"F0.wireOp",EDGE,"E141"),sQuery(id+"F0.wireOp",EDGE,"E142"),sQuery(id+"F0.wireOp",EDGE,"E143"),sQuery(id+"F0.wireOp",EDGE,"E144"),sQuery(id+"F0.wireOp",EDGE,"E145"),sQuery(id+"F0.wireOp",EDGE,"E146"),sQuery(id+"F0.wireOp",EDGE,"E147"),sQuery(id+"F0.wireOp",EDGE,"E148"),sQuery(id+"F0.wireOp",EDGE,"E149"),sQuery(id+"F0.wireOp",EDGE,"E150"),sQuery(id+"F0.wireOp",EDGE,"E151"),sQuery(id+"F0.wireOp",EDGE,"E152"),sQuery(id+"F0.wireOp",EDGE,"E153"),sQuery(id+"F0.wireOp",EDGE,"E154"),sQuery(id+"F0.wireOp",EDGE,"E155"),sQuery(id+"F0.wireOp",EDGE,"E156"),sQuery(id+"F0.wireOp",EDGE,"E157"),sQuery(id+"F0.wireOp",EDGE,"E158"),sQuery(id+"F0.wireOp",EDGE,"E159"),sQuery(id+"F0.wireOp",EDGE,"E160"),sQuery(id+"F0.wireOp",EDGE,"E161"),sQuery(id+"F0.wireOp",EDGE,"E162"),sQuery(id+"F0.wireOp",EDGE,"E163"),sQuery(id+"F0.wireOp",EDGE,"E164"),sQuery(id+"F0.wireOp",EDGE,"E165"),sQuery(id+"F0.wireOp",EDGE,"E166"),sQuery(id+"F0.wireOp",EDGE,"E167"),sQuery(id+"F0.wireOp",EDGE,"E168"),sQuery(id+"F0.wireOp",EDGE,"E169"),sQuery(id+"F0.wireOp",EDGE,"E170"),sQuery(id+"F0.wireOp",EDGE,"E171"),sQuery(id+"F0.wireOp",EDGE,"E172"),sQuery(id+"F0.wireOp",EDGE,"E173"),sQuery(id+"F0.wireOp",EDGE,"E174"),sQuery(id+"F0.wireOp",EDGE,"E175"),sQuery(id+"F0.wireOp",EDGE,"E176"),sQuery(id+"F0.wireOp",EDGE,"E177"),sQuery(id+"F0.wireOp",EDGE,"E178"),sQuery(id+"F0.wireOp",EDGE,"E179"),sQuery(id+"F0.wireOp",EDGE,"E180"),sQuery(id+"F0.wireOp",EDGE,"E181"),sQuery(id+"F0.wireOp",EDGE,"E182"),sQuery(id+"F0.wireOp",EDGE,"E183"),sQuery(id+"F0.wireOp",EDGE,"E184"),sQuery(id+"F0.wireOp",EDGE,"E185"),sQuery(id+"F0.wireOp",EDGE,"E186"),sQuery(id+"F0.wireOp",EDGE,"E187"),sQuery(id+"F0.wireOp",EDGE,"E188"),sQuery(id+"F0.wireOp",EDGE,"E189"),sQuery(id+"F0.wireOp",EDGE,"E190"),sQuery(id+"F0.wireOp",EDGE,"E191"),sQuery(id+"F0.wireOp",EDGE,"E192"),sQuery(id+"F0.wireOp",EDGE,"E193"),sQuery(id+"F0.wireOp",EDGE,"E194"),sQuery(id+"F0.wireOp",EDGE,"E195"),sQuery(id+"F0.wireOp",EDGE,"E196"),sQuery(id+"F0.wireOp",EDGE,"E197"),sQuery(id+"F0.wireOp",EDGE,"E198"),sQuery(id+"F0.wireOp",EDGE,"E199"),sQuery(id+"F0.wireOp",EDGE,"E200"),sQuery(id+"F0.wireOp",EDGE,"E201"),sQuery(id+"F0.wireOp",EDGE,"E202"),sQuery(id+"F0.wireOp",EDGE,"E203"),sQuery(id+"F0.wireOp",EDGE,"E204"),sQuery(id+"F0.wireOp",EDGE,"E205"),sQuery(id+"F0.wireOp",EDGE,"E206"),sQuery(id+"F0.wireOp",EDGE,"E207"),sQuery(id+"F0.wireOp",EDGE,"E208"),sQuery(id+"F0.wireOp",EDGE,"E209"),sQuery(id+"F0.wireOp",EDGE,"E210"),sQuery(id+"F0.wireOp",EDGE,"E211"),sQuery(id+"F0.wireOp",EDGE,"E212"),sQuery(id+"F0.wireOp",EDGE,"E213"),sQuery(id+"F0.wireOp",EDGE,"E214"),sQuery(id+"F0.wireOp",EDGE,"E215"),sQuery(id+"F0.wireOp",EDGE,"E216"),sQuery(id+"F0.wireOp",EDGE,"E217"),sQuery(id+"F0.wireOp",EDGE,"E218"),sQuery(id+"F0.wireOp",EDGE,"E219"),sQuery(id+"F0.wireOp",EDGE,"E220"),sQuery(id+"F0.wireOp",EDGE,"E221"),sQuery(id+"F0.wireOp",EDGE,"E222"),sQuery(id+"F0.wireOp",EDGE,"E223"),sQuery(id+"F0.wireOp",EDGE,"E224"),sQuery(id+"F0.wireOp",EDGE,"E225"),sQuery(id+"F0.wireOp",EDGE,"E226"),sQuery(id+"F0.wireOp",EDGE,"E227"),sQuery(id+"F0.wireOp",EDGE,"E228"),sQuery(id+"F0.wireOp",EDGE,"E229"),sQuery(id+"F0.wireOp",EDGE,"E230"),sQuery(id+"F0.wireOp",EDGE,"E231"),sQuery(id+"F0.wireOp",EDGE,"E232"),sQuery(id+"F0.wireOp",EDGE,"E233"),sQuery(id+"F0.wireOp",EDGE,"E234"),sQuery(id+"F0.wireOp",EDGE,"E235"),sQuery(id+"F0.wireOp",EDGE,"E236"),sQuery(id+"F0.wireOp",EDGE,"E237"),sQuery(id+"F0.wireOp",EDGE,"E238"),sQuery(id+"F0.wireOp",EDGE,"E239"),sQuery(id+"F0.wireOp",EDGE,"E240"),sQuery(id+"F0.wireOp",EDGE,"335e49da-e290-4d69-b9ee-bf74629cb29d"),sQuery(id+"F0.wireOp",EDGE,"a13d8cb5-f6a6-43dd-bdbe-38a068e7ae1e"),sQuery(id+"F0.wireOp",EDGE,"E241"),sQuery(id+"F0.wireOp",EDGE,"E242"),sQuery(id+"F0.wireOp",EDGE,"E243"),sQuery(id+"F0.wireOp",EDGE,"E244"),sQuery(id+"F0.wireOp",EDGE,"E245"),sQuery(id+"F0.wireOp",EDGE,"E246"),sQuery(id+"F0.wireOp",EDGE,"E247"),sQuery(id+"F0.wireOp",EDGE,"E248"),sQuery(id+"F0.wireOp",EDGE,"E249"),sQuery(id+"F0.wireOp",EDGE,"E250"),sQuery(id+"F0.wireOp",EDGE,"E251"),sQuery(id+"F0.wireOp",EDGE,"E252"),sQuery(id+"F0.wireOp",EDGE,"E253"),sQuery(id+"F0.wireOp",EDGE,"E254"),sQuery(id+"F0.wireOp",EDGE,"E255"),sQuery(id+"F0.wireOp",EDGE,"E256"),sQuery(id+"F0.wireOp",EDGE,"E257"),sQuery(id+"F0.wireOp",EDGE,"E258"),sQuery(id+"F0.wireOp",EDGE,"E259"),sQuery(id+"F0.wireOp",EDGE,"E260"),sQuery(id+"F0.wireOp",EDGE,"E261"),sQuery(id+"F0.wireOp",EDGE,"E262"),sQuery(id+"F0.wireOp",EDGE,"E263"),sQuery(id+"F0.wireOp",EDGE,"E264"),sQuery(id+"F0.wireOp",EDGE,"E265"),sQuery(id+"F0.wireOp",EDGE,"E266"),sQuery(id+"F0.wireOp",EDGE,"E267"),sQuery(id+"F0.wireOp",EDGE,"E268"),sQuery(id+"F0.wireOp",EDGE,"E269"),sQuery(id+"F0.wireOp",EDGE,"E270"),sQuery(id+"F0.wireOp",EDGE,"E271"),sQuery(id+"F0.wireOp",EDGE,"E272"),sQuery(id+"F0.wireOp",EDGE,"E273"),sQuery(id+"F0.wireOp",EDGE,"E274"),sQuery(id+"F0.wireOp",EDGE,"E275"),sQuery(id+"F0.wireOp",EDGE,"E276"),sQuery(id+"F0.wireOp",EDGE,"E277"),sQuery(id+"F0.wireOp",EDGE,"E278"),sQuery(id+"F0.wireOp",EDGE,"E279"),sQuery(id+"F0.wireOp",EDGE,"E280"),sQuery(id+"F0.wireOp",EDGE,"E281"),sQuery(id+"F0.wireOp",EDGE,"E282"),sQuery(id+"F0.wireOp",EDGE,"E283"),sQuery(id+"F0.wireOp",EDGE,"E284"),sQuery(id+"F0.wireOp",EDGE,"E285"),sQuery(id+"F0.wireOp",EDGE,"E286"),sQuery(id+"F0.wireOp",EDGE,"E287"),sQuery(id+"F0.wireOp",EDGE,"E288"),sQuery(id+"F0.wireOp",EDGE,"E289"),sQuery(id+"F0.wireOp",EDGE,"E290"),sQuery(id+"F0.wireOp",EDGE,"E291"),sQuery(id+"F0.wireOp",EDGE,"E292"),sQuery(id+"F0.wireOp",EDGE,"E293"),sQuery(id+"F0.wireOp",EDGE,"E294"),sQuery(id+"F0.wireOp",EDGE,"E295"),sQuery(id+"F0.wireOp",EDGE,"E296"),sQuery(id+"F0.wireOp",EDGE,"E297"),sQuery(id+"F0.wireOp",EDGE,"E298"),sQuery(id+"F0.wireOp",EDGE,"E299"),sQuery(id+"F0.wireOp",EDGE,"E300"),sQuery(id+"F0.wireOp",EDGE,"E301"),sQuery(id+"F0.wireOp",EDGE,"E302"),sQuery(id+"F0.wireOp",EDGE,"E303"),sQuery(id+"F0.wireOp",EDGE,"E304"),sQuery(id+"F0.wireOp",EDGE,"E305"),sQuery(id+"F0.wireOp",EDGE,"E306"),sQuery(id+"F0.wireOp",EDGE,"E307"),sQuery(id+"F0.wireOp",EDGE,"E308"),sQuery(id+"F0.wireOp",EDGE,"E309"),sQuery(id+"F0.wireOp",EDGE,"E310"),sQuery(id+"F0.wireOp",EDGE,"E311"),sQuery(id+"F0.wireOp",EDGE,"E312"),sQuery(id+"F0.wireOp",EDGE,"E313"),sQuery(id+"F0.wireOp",EDGE,"E314"),sQuery(id+"F0.wireOp",EDGE,"E315"),sQuery(id+"F0.wireOp",EDGE,"E316"),sQuery(id+"F0.wireOp",EDGE,"E317"),sQuery(id+"F0.wireOp",EDGE,"E318"),sQuery(id+"F0.wireOp",EDGE,"E319"),sQuery(id+"F0.wireOp",EDGE,"E320"),sQuery(id+"F0.wireOp",EDGE,"E321"),sQuery(id+"F0.wireOp",EDGE,"E322"),sQuery(id+"F0.wireOp",EDGE,"E323"),sQuery(id+"F0.wireOp",EDGE,"E324"),sQuery(id+"F0.wireOp",EDGE,"E325"),sQuery(id+"F0.wireOp",EDGE,"E326"),sQuery(id+"F0.wireOp",EDGE,"E327"),sQuery(id+"F0.wireOp",EDGE,"E328"),sQuery(id+"F0.wireOp",EDGE,"E329"),sQuery(id+"F0.wireOp",EDGE,"E330"),sQuery(id+"F0.wireOp",EDGE,"E331"),sQuery(id+"F0.wireOp",EDGE,"E332"),sQuery(id+"F0.wireOp",EDGE,"E333"),sQuery(id+"F0.wireOp",EDGE,"E334"),sQuery(id+"F0.wireOp",EDGE,"E335"),sQuery(id+"F0.wireOp",EDGE,"E336"),sQuery(id+"F0.wireOp",EDGE,"E337"),sQuery(id+"F0.wireOp",EDGE,"E338"),sQuery(id+"F0.wireOp",EDGE,"E339"),sQuery(id+"F0.wireOp",EDGE,"E340"),sQuery(id+"F0.wireOp",EDGE,"E341"),sQuery(id+"F0.wireOp",EDGE,"E342"),sQuery(id+"F0.wireOp",EDGE,"E343"),sQuery(id+"F0.wireOp",EDGE,"E344"),sQuery(id+"F0.wireOp",EDGE,"E345"),sQuery(id+"F0.wireOp",EDGE,"E346"),sQuery(id+"F0.wireOp",EDGE,"E347"),sQuery(id+"F0.wireOp",EDGE,"E349"),sQuery(id+"F0.wireOp",EDGE,"E350")])]});
            var Q1;
            Q1=sQuery(id+"F0.wireOp",VERTEX,"E349.center");
            transform(context, id + "F2", {"entities" : qUnion([Q0]), "transformType" : TransformType.SCALE_UNIFORMLY, "scale" : 0.6, "scalePoint" : qUnion([Q1]), "makeCopy" : false});
        }
    });
